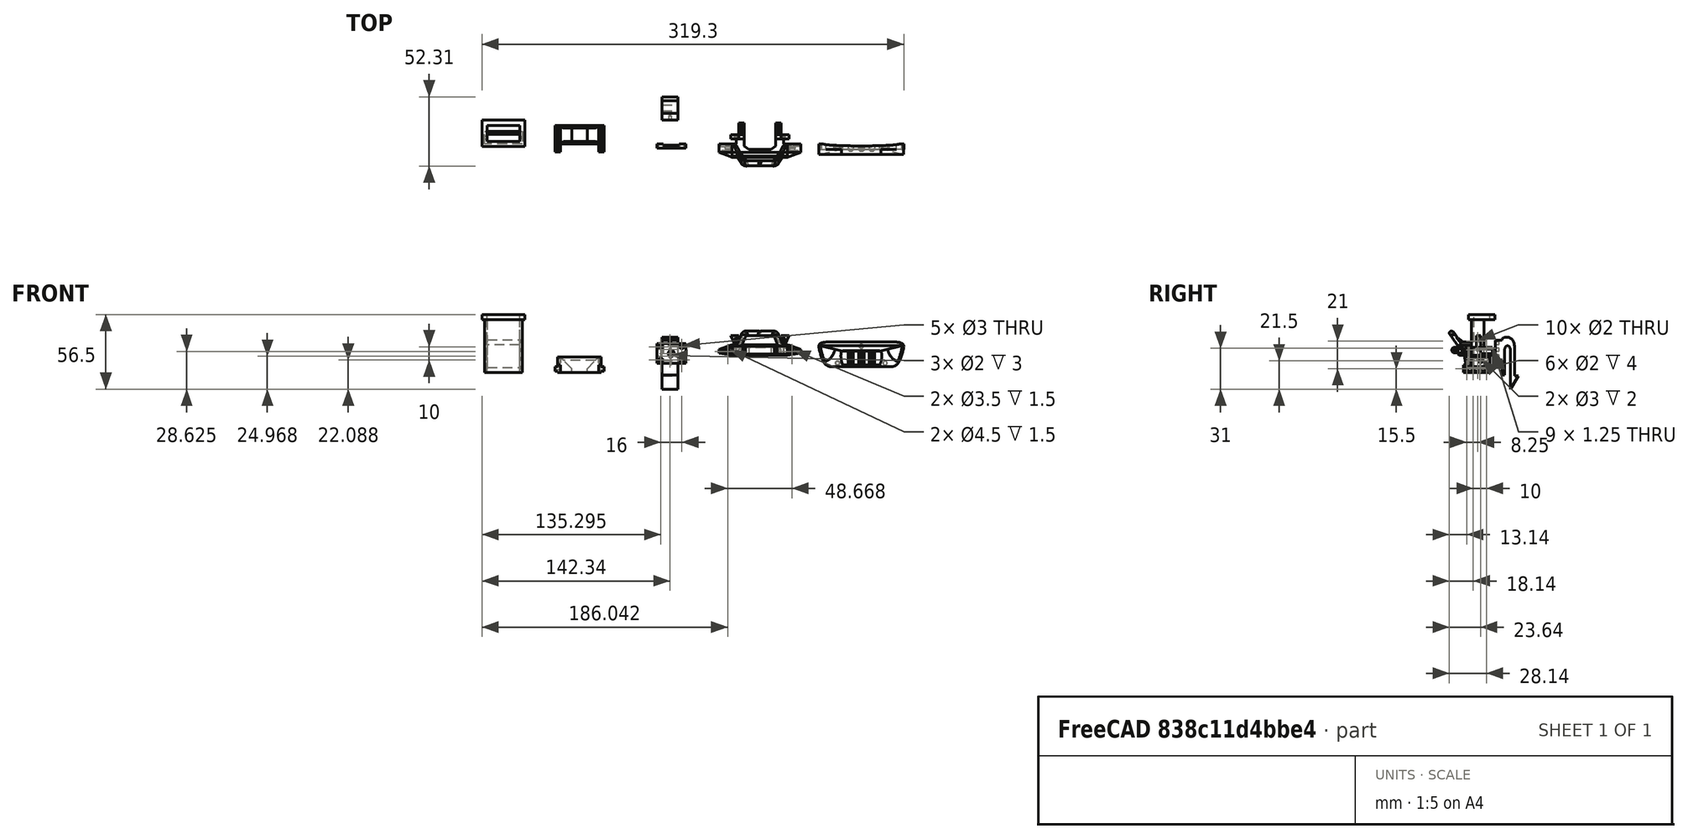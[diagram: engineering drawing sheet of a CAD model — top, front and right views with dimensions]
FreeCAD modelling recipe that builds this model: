
FCSTD DOCUMENT  (FreeCAD 0.21R33515 (Git))
Label: body-clips
License: All rights reserved
LicenseURL: https://en.wikipedia.org/wiki/All_rights_reserved
objects: Sketcher::SketchObject×33, PartDesign::Pocket×18, PartDesign::Pad×16, PartDesign::Body×6, PartDesign::Chamfer×6, PartDesign::Plane×4, PartDesign::Mirrored×4, Part::Part2DObjectPython×4, PartDesign::LinearPattern×2, PartDesign::AdditivePipe×2, Spreadsheet::Sheet×1, PartDesign::MultiTransform×1
note: 138 computed .brp shape members not serialized (recipe doc carries the construction recipe); baked Part::Feature solids carry a one-line shape summary decoded from their .brp

FEATURE [Spreadsheet::Sheet] Spreadsheet  label="param"
  cells = A1=common; A2(wall_thickness)==2 mm; A3(thread_diam)==3 mm; A4(rail_depth)==2 mm; A5(rail_height)==3.5 mm; A6(rail_length)==20 mm; A7(rail_diam)==2 mm; A8(body_width_front)==28 mm; A9(body_width_back)==33 mm; A10=chassis mount; B10=front; C10=back; A11(mount_body_depth)==14 mm; B11==14 mm; C11==14 mm; A12(mount_body_width)==33 mm; B12==28 mm; C12==33 mm; A13(mount_body_height)==12 mm; B13==12 mm; C13==12 mm; A14=tower; A15(tower_body_height)==40 mm; C15==40 mm; A16(tower_clip_depth)==10 mm; C16==10 mm; A17(tower_clip_height)==4 mm; C17==4 mm; A18=computed; A19(tower_body_width)==mount_body_width - 2 * wall_thickness - 0.5 mm; A20(tower_body_depth)==mount_body_depth - 2 * wall_thickness - 0.5 mm; A21(tower_clip_width)==tower_body_width + 2 * wall_thickness; A22=back plate; A23(bplate_width)==22 mm; A24(bplate_height)==15 mm; A25(bplate_thickness)==3 mm; A26(bplate_groove_depth)==1 mm; A27(bplate_groove_width)==12 mm; A28=clip; A29(clip_anker_depth)==5 mm; A30(clip_anker_height)==15 mm; A31(clip_depth)==10 mm; A32(clip_width)==12 mm; A33=grill; A34(grill_mount)==18 mm
FEATURE [Sketcher::SketchObject] Sketch
  FullyConstrained = true
  MapMode = 5
  Support = -> [XY_Plane]
  expr: Constraints[18] = <<param>>.wall_thickness
  expr: Constraints[19] = <<param>>.wall_thickness
  expr: Constraints[20] = <<param>>.wall_thickness
  expr: Constraints[21] = <<param>>.wall_thickness
  expr: Constraints[8] = Spreadsheet.mount_body_width
  expr: Constraints[9] = Spreadsheet.mount_body_depth
  sketch-geometry (8):
    g0: LineSegment StartX=0 StartY=14 StartZ=0 EndX=33 EndY=14 EndZ=0
    g1: LineSegment StartX=33 StartY=14 StartZ=0 EndX=33 EndY=0 EndZ=0
    g2: LineSegment StartX=33 StartY=0 StartZ=0 EndX=0 EndY=0 EndZ=0
    g3: LineSegment StartX=0 StartY=0 StartZ=0 EndX=0 EndY=14 EndZ=0
    g4: LineSegment StartX=2 StartY=12 StartZ=0 EndX=31 EndY=12 EndZ=0
    g5: LineSegment StartX=31 StartY=12 StartZ=0 EndX=31 EndY=2 EndZ=0
    g6: LineSegment StartX=31 StartY=2 StartZ=0 EndX=2 EndY=2 EndZ=0
    g7: LineSegment StartX=2 StartY=2 StartZ=0 EndX=2 EndY=12 EndZ=0
  constraints (23):
    c: Coincident(g0,g1)
    c: Coincident(g1,g2)
    c: Coincident(g2,g3)
    c: Coincident(g3,g0)
    c: Horizontal(g0)
    c: Horizontal(g2)
    c: Vertical(g1)
    c: Vertical(g3)
    c: DistanceX(g0,g0) = 33
    c: DistanceY(g3,g3) = 14
    c: Coincident(g4,g5)
    c: Coincident(g5,g6)
    c: Coincident(g6,g7)
    c: Coincident(g7,g4)
    c: Horizontal(g4)
    c: Horizontal(g6)
    c: Vertical(g5)
    c: Vertical(g7)
    c: DistanceX(g0,g4) = 2
    c: DistanceY(g4,g0) = 2
    c: DistanceX(g5,g1) = 2
    c: DistanceY(g1,g5) = 2
    c: Coincident(g2,g-1)
FEATURE [PartDesign::Pad] Pad  label="mount body"
  Direction = (0,0,1)
  Length = 12
  Length2 = 10
  Profile = -> Sketch
  ReferenceAxis = -> Sketch [N_Axis]
  Type = 0
  expr: Length = Spreadsheet.mount_body_height
FEATURE [Sketcher::SketchObject] Sketch001  label="rails"
  ExternalGeometry = -> [Pad]
  FullyConstrained = false
  MapMode = 5
  Placement = pos=(0,0,0) rot=(0.57735,-0.57735,-0.57735;2.0944rad)
  Support = -> [Pad]
  expr: Constraints[10] = (6 mm - Spreadsheet.rail_height) / 2
  expr: Constraints[8] = Spreadsheet.rail_height
  expr: Constraints[9] = Spreadsheet.rail_length
  sketch-geometry (4):
    g0: LineSegment StartX=-14 StartY=4.75 StartZ=0 EndX=6 EndY=4.75 EndZ=0
    g1: LineSegment StartX=6 StartY=4.75 StartZ=0 EndX=6 EndY=1.25 EndZ=0
    g2: LineSegment StartX=6 StartY=1.25 StartZ=0 EndX=-14 EndY=1.25 EndZ=0
    g3: LineSegment StartX=-14 StartY=1.25 StartZ=0 EndX=-14 EndY=4.75 EndZ=0
  constraints (11):
    c: Coincident(g0,g1)
    c: Coincident(g1,g2)
    c: Coincident(g2,g3)
    c: Coincident(g3,g0)
    c: Horizontal(g0)
    c: Horizontal(g2)
    c: Vertical(g1)
    c: Vertical(g3)
    c: DistanceY(g1,g1) = 3.5
    c: DistanceX(g0,g0) = 20
    c: DistanceY(g-6,g2) = 1.25
FEATURE [Sketcher::SketchObject] Sketch002
  ExternalGeometry = -> [Pad]
  FullyConstrained = true
  MapMode = 5
  Placement = pos=(0,0,0) rot=(0.57735,-0.57735,-0.57735;2.0944rad)
  Support = -> [Pad]
  expr: Constraints[8] = Spreadsheet.rail_length
  sketch-geometry (4):
    g0: LineSegment StartX=-14 StartY=6 StartZ=0 EndX=6 EndY=6 EndZ=0
    g1: LineSegment StartX=6 StartY=6 StartZ=0 EndX=6 EndY=0 EndZ=0
    g2: LineSegment StartX=6 StartY=0 StartZ=0 EndX=-14 EndY=0 EndZ=0
    g3: LineSegment StartX=-14 StartY=0 StartZ=0 EndX=-14 EndY=6 EndZ=0
  constraints (11):
    c: Coincident(g0,g1)
    c: Coincident(g1,g2)
    c: Coincident(g2,g3)
    c: Coincident(g3,g0)
    c: Horizontal(g0)
    c: Horizontal(g2)
    c: Vertical(g1)
    c: Vertical(g3)
    c: DistanceX(g0,g0) = 20
    c: DistanceY(g3,g3) = 6
    c: Coincident(g2,g-3)
FEATURE [PartDesign::Pad] Pad001  label="rail plate"
  BaseFeature = -> Pad
  Direction = (-1,0,0)
  Length = 0
  Length2 = 2
  Profile = -> Sketch002
  ReferenceAxis = -> Sketch002 [N_Axis]
  Type = 4
FEATURE [PartDesign::Pad] Pad002  label="rail"
  BaseFeature = -> Pad001
  Direction = (-1,0,0)
  Length = 2
  Length2 = 10
  Profile = -> Sketch001
  ReferenceAxis = -> Sketch001 [N_Axis]
  Type = 0
  expr: Length = Spreadsheet.rail_depth
FEATURE [Sketcher::SketchObject] Sketch003
  ExternalGeometry = -> [Pad002]
  FullyConstrained = true
  MapMode = 5
  Placement = pos=(0,0,0) rot=(0.57735,-0.57735,-0.57735;2.0944rad)
  Support = -> [Pad002]
  expr: Constraints[0] = <<param>>.thread_diam
  expr: Constraints[2] = Spreadsheet.mount_body_depth / 2
  sketch-geometry (1):
    g0: Circle CenterX=-7 CenterY=9 CenterZ=0 NormalX=0 NormalY=0 NormalZ=1 AngleXU=0 Radius=1.5
  constraints (3):
    c: Diameter(g0) = 3
    c: DistanceY(g0,g-5) = 3
    c: DistanceX(g0,g-5) = 7
FEATURE [PartDesign::Plane] DatumPlane  label="mount center plane"
  AttachmentOffset = pos=(0,0,-16.5) rot=(0,0,1;0rad)
  Length = 60
  MapMode = 5
  Placement = pos=(16.5,0,0) rot=(0.57735,-0.57735,-0.57735;2.0944rad)
  ResizeMode = 0
  Support = -> [Pad]
  Width = 60
  expr: .AttachmentOffset.Base.z = -Spreadsheet.mount_body_width / 2
FEATURE [Sketcher::SketchObject] Sketch004
  FullyConstrained = false
  MapMode = 5
  Placement = pos=(-2,0,0) rot=(0.57735,-0.57735,-0.57735;2.0944rad)
  expr: Constraints[0] = <<param>>.rail_diam
  sketch-geometry (4):
    g0: Circle CenterX=-11.5 CenterY=3 CenterZ=0 NormalX=0 NormalY=0 NormalZ=1 AngleXU=0 Radius=1
    g1: Circle CenterX=-6.5 CenterY=3 CenterZ=0 NormalX=0 NormalY=0 NormalZ=1 AngleXU=0 Radius=1
    g2: Circle CenterX=-1.5 CenterY=3 CenterZ=0 NormalX=0 NormalY=0 NormalZ=1 AngleXU=0 Radius=1
    g3: Circle CenterX=3.5 CenterY=3 CenterZ=0 NormalX=0 NormalY=0 NormalZ=1 AngleXU=0 Radius=1
  constraints (7):
    c: Diameter(g0) = 2
    c: Equal(g0,g1) = 2
    c: DistanceX(g0,g1) = 5
    c: Equal(g0,g2) = 2
    c: Equal(g2,g3) = 2
    c: DistanceX(g2,g3) = 5
    c: DistanceX(g1,g2) = 5
FEATURE [Sketcher::SketchObject] Sketch010
  FullyConstrained = false
  MapMode = 5
  Support = -> [XY_Plane002]
  expr: Constraints[10] = <<param>>.tower_body_depth
  expr: Constraints[19] = <<param>>.wall_thickness
  expr: Constraints[20] = <<param>>.wall_thickness
  expr: Constraints[21] = <<param>>.wall_thickness
  expr: Constraints[22] = <<param>>.wall_thickness
  expr: Constraints[9] = <<param>>.tower_body_width
  sketch-geometry (8):
    g0: LineSegment StartX=-55.3396 StartY=9.5 StartZ=0 EndX=-26.8396 EndY=9.5 EndZ=0
    g1: LineSegment StartX=-26.8396 StartY=9.5 StartZ=0 EndX=-26.8396 EndY=0 EndZ=0
    g2: LineSegment StartX=-26.8396 StartY=0 StartZ=0 EndX=-55.3396 EndY=0 EndZ=0
    g3: LineSegment StartX=-55.3396 StartY=0 StartZ=0 EndX=-55.3396 EndY=9.5 EndZ=0
    g4: LineSegment StartX=-53.3396 StartY=7.5 StartZ=0 EndX=-28.8396 EndY=7.5 EndZ=0
    g5: LineSegment StartX=-28.8396 StartY=7.5 StartZ=0 EndX=-28.8396 EndY=2 EndZ=0
    g6: LineSegment StartX=-28.8396 StartY=2 StartZ=0 EndX=-53.3396 EndY=2 EndZ=0
    g7: LineSegment StartX=-53.3396 StartY=2 StartZ=0 EndX=-53.3396 EndY=7.5 EndZ=0
  constraints (23):
    c: Coincident(g0,g1)
    c: Coincident(g1,g2)
    c: Coincident(g2,g3)
    c: Coincident(g3,g0)
    c: Horizontal(g0)
    c: Horizontal(g2)
    c: Vertical(g1)
    c: Vertical(g3)
    c: PointOnObject(g1,g-1)
    c: DistanceX(g0,g0) = 28.5
    c: DistanceY(g3,g3) = 9.5
    c: Coincident(g4,g5)
    c: Coincident(g5,g6)
    c: Coincident(g6,g7)
    c: Coincident(g7,g4)
    c: Horizontal(g4)
    c: Horizontal(g6)
    c: Vertical(g5)
    c: Vertical(g7)
    c: DistanceX(g0,g4) = 2
    c: DistanceX(g4,g0) = 2
    c: DistanceY(g4,g0) = 2
    c: DistanceY(g1,g5) = 2
FEATURE [PartDesign::Pad] Pad006  label="tower body"
  Direction = (0,0,1)
  Length = 40
  Length2 = 10
  Profile = -> Sketch010
  ReferenceAxis = -> Sketch010 [N_Axis]
  Refine = true
  Type = 0
  expr: Length = <<param>>.tower_body_height
FEATURE [PartDesign::Plane] DatumPlane002  label="tower center plane"
  AttachmentOffset = pos=(0,0,-14.25) rot=(0,0,1;0rad)
  Length = 61.7473
  MapMode = 5
  Placement = pos=(-41.0896,0,0) rot=(0.57735,-0.57735,-0.57735;2.0944rad)
  ResizeMode = 0
  Support = -> [Pad006]
  Width = 80.7473
  expr: .AttachmentOffset.Base.z = -<<param>>.tower_body_width / 2
FEATURE [Sketcher::SketchObject] Sketch011
  ExternalGeometry = -> [Pad006]
  FullyConstrained = true
  MapMode = 5
  Placement = pos=(0,0,40) rot=(0,0,1;0rad)
  Support = -> [Pad006]
  expr: Constraints[16] = <<param>>.wall_thickness * 2
  expr: Constraints[17] = <<param>>.wall_thickness * 2
  expr: Constraints[18] = <<param>>.wall_thickness * 2
  expr: Constraints[19] = <<param>>.wall_thickness * 2
  expr: Constraints[20] = <<param>>.tower_clip_depth + 5 * <<param>>.wall_thickness
  expr: Constraints[21] = <<param>>.tower_clip_width
  sketch-geometry (8):
    g0: LineSegment StartX=-57.3396 StartY=18 StartZ=0 EndX=-24.8396 EndY=18 EndZ=0
    g1: LineSegment StartX=-24.8396 StartY=18 StartZ=0 EndX=-24.8396 EndY=-2 EndZ=0
    g2: LineSegment StartX=-24.8396 StartY=-2 StartZ=0 EndX=-57.3396 EndY=-2 EndZ=0
    g3: LineSegment StartX=-57.3396 StartY=-2 StartZ=0 EndX=-57.3396 EndY=18 EndZ=0
    g4: LineSegment StartX=-53.3396 StartY=14 StartZ=0 EndX=-28.8396 EndY=14 EndZ=0
    g5: LineSegment StartX=-28.8396 StartY=14 StartZ=0 EndX=-28.8396 EndY=2 EndZ=0
    g6: LineSegment StartX=-28.8396 StartY=2 StartZ=0 EndX=-53.3396 EndY=2 EndZ=0
    g7: LineSegment StartX=-53.3396 StartY=2 StartZ=0 EndX=-53.3396 EndY=14 EndZ=0
  constraints (23):
    c: Coincident(g0,g1)
    c: Coincident(g1,g2)
    c: Coincident(g2,g3)
    c: Coincident(g3,g0)
    c: Horizontal(g0)
    c: Horizontal(g2)
    c: Vertical(g1)
    c: Vertical(g3)
    c: Coincident(g4,g5)
    c: Coincident(g5,g6)
    c: Coincident(g6,g7)
    c: Coincident(g7,g4)
    c: Horizontal(g4)
    c: Horizontal(g6)
    c: Vertical(g5)
    c: Vertical(g7)
    c: DistanceX(g0,g4) = 4
    c: DistanceX(g4,g0) = 4
    c: DistanceY(g4,g0) = 4
    c: DistanceY(g1,g5) = 4
    c: DistanceY(g1,g1) = 20
    c: DistanceX(g0,g0) = 32.5
    c: Coincident(g5,g-5)
FEATURE [PartDesign::Pad] Pad007  label="tower clip"
  BaseFeature = -> Pad006
  Direction = (0,0,1)
  Length = 4
  Length2 = 10
  Profile = -> Sketch011
  ReferenceAxis = -> Sketch011 [N_Axis]
  Refine = true
  Type = 0
  expr: Length = <<param>>.tower_clip_height
FEATURE [Sketcher::SketchObject] Sketch012
  ExternalGeometry = -> [Pad006]
  FullyConstrained = true
  MapMode = 5
  Placement = pos=(0,9.5,0) rot=(0,0.707107,0.707107;3.14159rad)
  Support = -> [Pad007]
  expr: Constraints[10] = <<param>>.wall_thickness
  expr: Constraints[20] = <<param>>.tower_body_height - 15 mm - 8 mm
  expr: Constraints[21] = <<param>>.tower_body_width - 2 * <<param>>.wall_thickness
  expr: Constraints[8] = <<param>>.tower_body_width - 2 * <<param>>.wall_thickness
  sketch-geometry (8):
    g0: LineSegment StartX=28.8396 StartY=40 StartZ=0 EndX=53.3396 EndY=40 EndZ=0
    g1: LineSegment StartX=53.3396 StartY=40 StartZ=0 EndX=53.3396 EndY=25 EndZ=0
    g2: LineSegment StartX=53.3396 StartY=25 StartZ=0 EndX=28.8396 EndY=25 EndZ=0
    g3: LineSegment StartX=28.8396 StartY=25 StartZ=0 EndX=28.8396 EndY=40 EndZ=0
    g4: LineSegment StartX=28.8396 StartY=21 StartZ=0 EndX=53.3396 EndY=21 EndZ=0
    g5: LineSegment StartX=53.3396 StartY=21 StartZ=0 EndX=53.3396 EndY=4 EndZ=0
    g6: LineSegment StartX=53.3396 StartY=4 StartZ=0 EndX=28.8396 EndY=4 EndZ=0
    g7: LineSegment StartX=28.8396 StartY=4 StartZ=0 EndX=28.8396 EndY=21 EndZ=0
  constraints (24):
    c: Coincident(g0,g1)
    c: Coincident(g1,g2)
    c: Coincident(g2,g3)
    c: Coincident(g3,g0)
    c: Horizontal(g0)
    c: Horizontal(g2)
    c: Vertical(g1)
    c: Vertical(g3)
    c: DistanceX(g0,g0) = 24.5
    c: DistanceY(g3,g3) = 15
    c: DistanceX(g-3,g0) = 2
    c: DistanceY(g0,g-3) = 0
    c: Coincident(g4,g5)
    c: Coincident(g5,g6)
    c: Coincident(g6,g7)
    c: Coincident(g7,g4)
    c: Horizontal(g4)
    c: Horizontal(g6)
    c: Vertical(g5)
    c: Vertical(g7)
    c: DistanceY(g7,g7) = 17
    c: DistanceX(g4,g4) = 24.5
    c: DistanceY(g4,g2) = 4
    c: DistanceX(g4,g2) = 0
FEATURE [PartDesign::Pocket] Pocket004  label="tower clip cutout"
  BaseFeature = -> Pad007
  Direction = (0,-1,2e-16)
  Length = 5
  Length2 = 5
  Profile = -> Sketch012
  ReferenceAxis = -> Sketch012 [N_Axis]
  Refine = true
  Type = 0
FEATURE [Sketcher::SketchObject] Sketch013
  FullyConstrained = true
  MapMode = 5
  Placement = pos=(-55.3396,0,0) rot=(0.57735,-0.57735,-0.57735;2.0944rad)
  Support = -> [Pocket004]
  expr: Constraints[0] = <<param>>.rail_diam
  expr: Constraints[1] = <<param>>.tower_body_depth / 2
  sketch-geometry (1):
    g0: Circle CenterX=-4.75 CenterY=4 CenterZ=0 NormalX=0 NormalY=0 NormalZ=1 AngleXU=0 Radius=1
  constraints (3):
    c: Diameter(g0) = 2
    c: DistanceX(g0,g-1) = 4.75
    c: DistanceY(g-1,g0) = 4
FEATURE [PartDesign::Pocket] Pocket005  label="tower drills"
  BaseFeature = -> Pocket004
  Direction = (1,0,0)
  Length = 5
  Length2 = 5
  Profile = -> Sketch013
  ReferenceAxis = -> Sketch013 [N_Axis]
  Refine = true
  Type = 0
FEATURE [PartDesign::LinearPattern] LinearPattern
  Direction = -> Z_Axis002
  Length = 20
  Occurrences = 4
  Refine = true
  expr: Length = <<param>>.tower_body_height - 20 mm
FEATURE [PartDesign::Mirrored] Mirrored002
  MirrorPlane = -> DatumPlane002
  Refine = true
FEATURE [PartDesign::MultiTransform] MultiTransform
  BaseFeature = -> Pocket005
  Originals = -> [Pocket005]
  Refine = true
  Transformations = -> [LinearPattern,Mirrored002]
FEATURE [PartDesign::Body] Body002  label="tower"
  Group = -> [Sketch010,Pad006,DatumPlane002,Sketch011,Pad007,Sketch012,Pocket004,Sketch013,Pocket005,MultiTransform,LinearPattern,Mirrored002]
  Origin = -> Origin002
  Tip = -> MultiTransform
FEATURE [Sketcher::SketchObject] Sketch014
  FullyConstrained = false
  MapMode = 5
  Placement = pos=(0,0,0) rot=(1,0,0;1.5708rad)
  Support = -> [XZ_Plane003]
  expr: Constraints[13] = (<<param>>.bplate_width - 16 mm) / 2
  expr: Constraints[14] = (<<param>>.bplate_height - 10 mm) / 2
  expr: Constraints[15] = (<<param>>.bplate_height - 10 mm) / 2
  expr: Constraints[19] = (<<param>>.bplate_width - 16 mm) / 2
  expr: Constraints[22] = <<param>>.thread_diam
  expr: Constraints[23] = <<param>>.bplate_width / 2
  expr: Constraints[24] = <<param>>.bplate_height / 2
  expr: Constraints[8] = <<param>>.bplate_width
  expr: Constraints[9] = <<param>>.bplate_height
  sketch-geometry (9):
    g0: LineSegment StartX=10.9554 StartY=22.0881 StartZ=0 EndX=32.9554 EndY=22.0881 EndZ=0
    g1: LineSegment StartX=32.9554 StartY=22.0881 StartZ=0 EndX=32.9554 EndY=7.08806 EndZ=0
    g2: LineSegment StartX=32.9554 StartY=7.08806 StartZ=0 EndX=10.9554 EndY=7.08806 EndZ=0
    g3: LineSegment StartX=10.9554 StartY=7.08806 StartZ=0 EndX=10.9554 EndY=22.0881 EndZ=0
    g4: Circle CenterX=13.9554 CenterY=19.5881 CenterZ=0 NormalX=0 NormalY=0 NormalZ=1 AngleXU=0 Radius=1.5
    g5: Circle CenterX=29.9554 CenterY=19.5881 CenterZ=0 NormalX=0 NormalY=0 NormalZ=1 AngleXU=0 Radius=1.5
    g6: Circle CenterX=13.9554 CenterY=9.58806 CenterZ=0 NormalX=0 NormalY=0 NormalZ=1 AngleXU=0 Radius=1.5
    g7: Circle CenterX=29.9554 CenterY=9.58806 CenterZ=0 NormalX=0 NormalY=0 NormalZ=1 AngleXU=0 Radius=1.5
    g8: Circle CenterX=21.9554 CenterY=14.5881 CenterZ=0 NormalX=0 NormalY=0 NormalZ=1 AngleXU=0 Radius=1.5
  constraints (25):
    c: Coincident(g0,g1)
    c: Coincident(g1,g2)
    c: Coincident(g2,g3)
    c: Coincident(g3,g0)
    c: Horizontal(g0)
    c: Horizontal(g2)
    c: Vertical(g1)
    c: Vertical(g3)
    c: DistanceX(g0,g0) = 22
    c: DistanceY(g1,g1) = 15
    c: Diameter(g4) = 3
    c: Equal(g4,g5) = 3
    c: DistanceX(g4,g5) = 16
    c: DistanceX(g0,g4) = 3
    c: DistanceY(g4,g0) = 2.5
    c: DistanceY(g5,g0) = 2.5
    c: Equal(g4,g6) = 3
    c: Equal(g6,g7) = 3
    c: DistanceX(g6,g7) = 16
    c: DistanceX(g2,g6) = 3
    c: DistanceY(g6,g4) = 10
    c: DistanceY(g7,g5) = 10
    c: Diameter(g8) = 3
    c: DistanceX(g0,g8) = 11
    c: DistanceY(g8,g0) = 7.5
FEATURE [PartDesign::Pad] Pad008
  Direction = (0,-1,-2e-16)
  Length = 3
  Length2 = 10
  Placement = pos=(0,0,0) rot=(1,0,0;1.5708rad)
  Profile = -> Sketch014
  ReferenceAxis = -> Sketch014 [N_Axis]
  Refine = true
  Type = 0
  expr: Length = <<param>>.bplate_thickness
FEATURE [Sketcher::SketchObject] Sketch015
  ExternalGeometry = -> [Pad008]
  FullyConstrained = false
  MapMode = 5
  Placement = pos=(0,0,0) rot=(-1,0,0;1.5708rad)
  Support = -> [Pad008]
  expr: Constraints[8] = <<param>>.bplate_height
  expr: Constraints[9] = <<param>>.bplate_groove_width
  sketch-geometry (4):
    g0: LineSegment StartX=15.9554 StartY=-7.08806 StartZ=0 EndX=27.9554 EndY=-7.08806 EndZ=0
    g1: LineSegment StartX=27.9554 StartY=-7.08806 StartZ=0 EndX=27.9554 EndY=-22.0881 EndZ=0
    g2: LineSegment StartX=27.9554 StartY=-22.0881 StartZ=0 EndX=15.9554 EndY=-22.0881 EndZ=0
    g3: LineSegment StartX=15.9554 StartY=-22.0881 StartZ=0 EndX=15.9554 EndY=-7.08806 EndZ=0
  constraints (11):
    c: Coincident(g0,g1)
    c: Coincident(g1,g2)
    c: Coincident(g2,g3)
    c: Coincident(g3,g0)
    c: Horizontal(g0)
    c: Horizontal(g2)
    c: Vertical(g1)
    c: Vertical(g3)
    c: DistanceY(g3,g3) = 15
    c: DistanceX(g0,g0) = 12
    c: DistanceY(g0,g-3) = 0
FEATURE [PartDesign::Pocket] Pocket006
  BaseFeature = -> Pad008
  Direction = (0,-1,-2e-16)
  Length = 1
  Length2 = 5
  Placement = pos=(0,0,0) rot=(1,0,0;1.5708rad)
  Profile = -> Sketch015
  ReferenceAxis = -> Sketch015 [N_Axis]
  Refine = true
  Type = 0
  expr: Length = <<param>>.bplate_groove_depth
FEATURE [Sketcher::SketchObject] Sketch016
  FullyConstrained = false
  MapMode = 5
  Placement = pos=(0,0,0) rot=(0.57735,0.57735,0.57735;2.0944rad)
  Support = -> [YZ_Plane004]
  expr: Constraints[12] = <<param>>.clip_anker_depth
  expr: Constraints[13] = <<param>>.clip_anker_height
  expr: Constraints[47] = <<param>>.mount_body_height
  expr: Constraints[48] = <<param>>.tower_body_depth
  expr: Constraints[56] = <<param>>.wall_thickness
  sketch-geometry (26):
    g0: LineSegment StartX=18.1651 StartY=24.4988 StartZ=0 EndX=23.1651 EndY=24.4988 EndZ=0
    g1: LineSegment StartX=23.1651 StartY=9.49883 StartZ=0 EndX=18.1651 EndY=9.49883 EndZ=0
    g2: LineSegment StartX=18.1651 StartY=9.49883 StartZ=0 EndX=18.1651 EndY=24.4988 EndZ=0
    g3: LineSegment StartX=32.6651 StartY=20.0525 StartZ=0 EndX=32.6651 EndY=-2.50117 EndZ=0
    g4: LineSegment StartX=32.6651 StartY=-2.50117 StartZ=0 EndX=35.6651 EndY=-2.50117 EndZ=0
    g5: LineSegment StartX=35.6651 StartY=-2.50117 StartZ=0 EndX=29.6651 EndY=-12.5012 EndZ=0
    g6: LineSegment StartX=29.6651 StartY=-12.5012 StartZ=0 EndX=29.6651 EndY=16.896 EndZ=0
    g7: GeomPoint X=23.1651 Y=24.4988 Z=0
    g8: GeomPoint X=26.4127 Y=26.9246 Z=0
    g9: GeomPoint X=32.6651 Y=20.0525 Z=0
    g10: BSplineCurve PolesCount=4 KnotsCount=2 Degree=3 IsPeriodic=0
    g11-g14: Circle x4 (B-spline internal-alignment scaffolding for g10; pole/knot coordinates omitted)
    g15: GeomPoint X=25.1651 Y=16.5755 Z=0
    g16: GeomPoint X=27.311 Y=20.3862 Z=0
    g17: GeomPoint X=29.6651 Y=16.896 Z=0
    g18: BSplineCurve PolesCount=4 KnotsCount=2 Degree=3 IsPeriodic=0
    g19-g22: Circle x4 (B-spline internal-alignment scaffolding for g18; pole/knot coordinates omitted)
    g23: LineSegment StartX=23.1651 StartY=9.49883 StartZ=0 EndX=23.1651 EndY=-1.80872 EndZ=0
    g24: LineSegment StartX=23.1651 StartY=-1.80872 StartZ=0 EndX=25.1651 EndY=-1.80872 EndZ=0
    g25: LineSegment StartX=25.1651 StartY=-1.80872 StartZ=0 EndX=25.1651 EndY=16.5755 EndZ=0
  constraints (58):
    c: Coincident(g1,g2)
    c: Coincident(g2,g0)
    c: Horizontal(g0)
    c: Horizontal(g1)
    c: Vertical(g2)
    c: Vertical(g3)
    c: Coincident(g4,g3)
    c: Horizontal(g4)
    c: Coincident(g5,g4)
    c: Coincident(g6,g5)
    c: Vertical(g6)
    c: DistanceX(g4,g4) = 3
    c: DistanceX(g0,g0) = 5
    c: DistanceY(g2,g2) = 15
    c: DistanceX(g6,g3) = 3
    c: Coincident(g10,g0)
    c: Coincident(g10,g3)
    c: InternalAlignment(g7,g10)
    c: PointOnObject(g8,g10)
    c: InternalAlignment(g9,g10)
    c: InternalAlignment(g11,g10)
    c: Weight(g11) = 1
    c: InternalAlignment(g12,g10)
    c: Equal(g12,g11)
    c: InternalAlignment(g13,g10)
    c: Equal(g13,g11)
    c: InternalAlignment(g14,g10)
    c: Equal(g14,g11)
    c: DistanceY(g12,g13) = 0
    c: DistanceX(g12,g0) = 0
    c: DistanceX(g3,g13) = 0
    c: Coincident(g18,g6)
    c: InternalAlignment(g15,g18)
    c: PointOnObject(g16,g18)
    c: InternalAlignment(g17,g18)
    c: InternalAlignment(g19,g18)
    c: Weight(g19) = 1
    c: InternalAlignment(g20,g18)
    c: Equal(g20,g19)
    c: InternalAlignment(g21,g18)
    c: Equal(g21,g19)
    c: InternalAlignment(g22,g18)
    c: Equal(g22,g19)
    c: DistanceY(g21,g20) = 0
    c: DistanceX(g18,g20) = 0
    c: DistanceX(g21,g6) = 0
    c: DistanceY(g5,g3) = 10
    c: DistanceY(g3,g1) = 12
    c: DistanceX(g1,g9) = 9.5
    c: Coincident(g23,g1)
    c: Vertical(g23)
    c: Coincident(g24,g23)
    c: Horizontal(g24)
    c: Coincident(g25,g18)
    c: Vertical(g25)
    c: Coincident(g25,g24)
    c: DistanceX(g24,g24) = 2
    c: DistanceX(g0,g1) = 0
FEATURE [PartDesign::Pad] Pad009
  Direction = (1,-2e-16,3e-16)
  Length = 12
  Length2 = 10
  Placement = pos=(0,0,0) rot=(0.57735,0.57735,0.57735;2.0944rad)
  Profile = -> Sketch016
  ReferenceAxis = -> Sketch016 [N_Axis]
  Refine = true
  Type = 0
  expr: Length = <<param>>.clip_width
FEATURE [PartDesign::Chamfer] Chamfer
  Angle = 45
  Base = -> Pocket006 [Face13]
  BaseFeature = -> Pocket006
  ChamferType = 2
  FlipDirection = false
  Placement = pos=(0,0,0) rot=(1,0,0;1.5708rad)
  Refine = true
  Size = 0.8
  Size2 = 1
  SupportTransform = false
  UseAllEdges = false
FEATURE [PartDesign::Body] Body003  label="back plate"
  Group = -> [Sketch014,Pad008,Sketch015,Pocket006,Chamfer]
  Origin = -> Origin003
  Placement = pos=(64,0,0) rot=(0,0,1;0rad)
  Tip = -> Chamfer
FEATURE [Sketcher::SketchObject] Sketch017
  ExternalGeometry = -> [Pad009]
  FullyConstrained = false
  MapMode = 5
  Placement = pos=(8e-15,18.1651,-4e-15) rot=(-0.57735,-0.57735,0.57735;4.18879rad)
  Support = -> [Pad009]
  expr: Constraints[0] = <<param>>.rail_diam
  expr: Constraints[1] = <<param>>.clip_width / 2
  sketch-geometry (1):
    g0: Circle CenterX=-22.4675 CenterY=6 CenterZ=0 NormalX=0 NormalY=0 NormalZ=1 AngleXU=0 Radius=1
  constraints (2):
    c: Diameter(g0) = 2
    c: DistanceY(g0,g-3) = 6
FEATURE [PartDesign::Pocket] Pocket007
  BaseFeature = -> Pad009
  Direction = (4e-16,1,-2e-16)
  Length = 3
  Length2 = 5
  Placement = pos=(0,0,0) rot=(0.57735,0.57735,0.57735;2.0944rad)
  Profile = -> Sketch017
  ReferenceAxis = -> Sketch017 [N_Axis]
  Refine = true
  Type = 0
FEATURE [PartDesign::LinearPattern] LinearPattern001
  BaseFeature = -> Pocket007
  Direction = -> Z_Axis004
  Length = 15
  Occurrences = 4
  Originals = -> [Pocket007]
  Placement = pos=(0,0,0) rot=(0.57735,0.57735,0.57735;2.0944rad)
  Refine = true
  Reversed = true
  expr: Length = <<param>>.clip_anker_height
FEATURE [PartDesign::Body] Body004  label="clip"
  Group = -> [Sketch016,Pad009,Sketch017,Pocket007,LinearPattern001]
  Origin = -> Origin004
  Placement = pos=(79,0,0) rot=(0,0,1;0rad)
  Tip = -> LinearPattern001
FEATURE [Sketcher::SketchObject] Sketch018
  FullyConstrained = false
  MapMode = 5
  Placement = pos=(0,0,0) rot=(1,0,0;1.5708rad)
  Support = -> [XZ_Plane005]
  sketch-geometry (17):
    g0: LineSegment StartX=229.786 StartY=23.4729 StartZ=0 EndX=250.786 EndY=23.4729 EndZ=0
    g1: LineSegment StartX=229.786 StartY=4.47292 StartZ=0 EndX=250.786 EndY=4.47292 EndZ=0
    g2: LineSegment StartX=229.786 StartY=4.47292 StartZ=0 EndX=229.786 EndY=23.4729 EndZ=0
    g3: LineSegment StartX=250.786 StartY=23.4729 StartZ=0 EndX=260.786 EndY=23.4729 EndZ=0
    g4: LineSegment StartX=260.786 StartY=23.4729 StartZ=0 EndX=260.786 EndY=4.47292 EndZ=0
    g5: LineSegment StartX=250.786 StartY=4.47292 StartZ=0 EndX=260.786 EndY=4.47292 EndZ=0
    g6-g9: GeomPoint x4 (B-spline internal-alignment scaffolding for g10; pole/knot coordinates omitted)
    g10: BSplineCurve PolesCount=6 KnotsCount=4 Degree=3 IsPeriodic=0
    g11-g16: Circle x6 (B-spline internal-alignment scaffolding for g10; pole/knot coordinates omitted)
  constraints (31):
    c: Horizontal(g0)
    c: Horizontal(g1)
    c: DistanceY(g1,g0) = 19
    c: Coincident(g2,g1)
    c: Coincident(g2,g0)
    c: Vertical(g2)
    c: DistanceX(g0,g0) = 21
    c: DistanceX(g1,g1) = 21
    c: Coincident(g3,g0)
    c: Horizontal(g3)
    c: Coincident(g4,g3)
    c: Vertical(g4)
    c: Coincident(g5,g1)
    c: Coincident(g5,g4)
    c: Horizontal(g5)
    c: DistanceX(g5,g5) = 10
    c: Coincident(g10,g0)
    c: Coincident(g10,g1)
    c: InternalAlignment(g6-g9 -> g10) x4
    c: InternalAlignment(g11,g10)
    c: Weight(g11) = 1
    c: InternalAlignment(g12,g10)
    c: Equal(g12,g11)
    c: InternalAlignment(g13,g10)
    c: Equal(g13,g11)
    c: InternalAlignment(g14,g10)
    c: Equal(g14,g11)
    c: InternalAlignment(g15,g10)
    c: Equal(g15,g11)
    c: InternalAlignment(g16,g10)
    c: Equal(g16,g11)
FEATURE [PartDesign::Pad] Pad010  label="grill base"
  Direction = (0,-1,-2e-16)
  Length = 4
  Length2 = 10
  Placement = pos=(0,0,0) rot=(1,0,0;1.5708rad)
  Profile = -> Sketch018
  ReferenceAxis = -> Sketch018 [N_Axis]
  Refine = true
  Type = 0
FEATURE [Sketcher::SketchObject] Sketch019
  ExternalGeometry = -> [Pad010]
  FullyConstrained = false
  MapMode = 5
  Placement = pos=(0,-4,-9e-16) rot=(1,0,0;1.5708rad)
  Support = -> [Pad010]
  sketch-geometry (10):
    g0: LineSegment StartX=229.786 StartY=21.9959 StartZ=0 EndX=243.834 EndY=21.9959 EndZ=0
    g1: LineSegment StartX=243.834 StartY=5.89636 StartZ=0 EndX=229.786 EndY=5.89636 EndZ=0
    g2: LineSegment StartX=229.786 StartY=5.89636 StartZ=0 EndX=229.786 EndY=21.9959 EndZ=0
    g3: GeomPoint X=243.834 Y=21.9959 Z=0
    g4: GeomPoint X=243.834 Y=5.89636 Z=0
    g5: BSplineCurve PolesCount=4 KnotsCount=2 Degree=3 IsPeriodic=0
    g6-g9: Circle x4 (B-spline internal-alignment scaffolding for g5; pole/knot coordinates omitted)
  constraints (18):
    c: Coincident(g1,g2)
    c: Coincident(g2,g0)
    c: Horizontal(g0)
    c: Horizontal(g1)
    c: Vertical(g2)
    c: Coincident(g5,g0)
    c: Coincident(g5,g1)
    c: InternalAlignment(g3,g5)
    c: InternalAlignment(g4,g5)
    c: InternalAlignment(g6,g5)
    c: Weight(g6) = 1
    c: InternalAlignment(g7,g5)
    c: Equal(g7,g6)
    c: InternalAlignment(g8,g5)
    c: Equal(g8,g6)
    c: InternalAlignment(g9,g5)
    c: Equal(g9,g6)
    c: DistanceX(g0,g-3) = 0
FEATURE [Sketcher::SketchObject] Sketch020
  FullyConstrained = false
  MapMode = 5
  Placement = pos=(0,-4,-9e-16) rot=(1,0,0;1.5708rad)
  Support = -> [Pad010]
  sketch-geometry (18):
    g0-g3: GeomPoint x4 (B-spline internal-alignment scaffolding for g4; pole/knot coordinates omitted)
    g4: BSplineCurve PolesCount=6 KnotsCount=4 Degree=3 IsPeriodic=0
    g5-g10: Circle x6 (B-spline internal-alignment scaffolding for g4; pole/knot coordinates omitted)
    g11: GeomPoint X=248.794 Y=21.8316 Z=0
    g12: GeomPoint X=256.494 Y=8.78724 Z=0
    g13: BSplineCurve PolesCount=4 KnotsCount=2 Degree=3 IsPeriodic=0
    g14-g17: Circle x4 (B-spline internal-alignment scaffolding for g13; pole/knot coordinates omitted)
  constraints (25):
    c: InternalAlignment(g0-g3 -> g4) x4
    c: InternalAlignment(g5,g4)
    c: Weight(g5) = 1
    c: InternalAlignment(g6,g4)
    c: Equal(g6,g5)
    c: InternalAlignment(g7,g4)
    c: Equal(g7,g5)
    c: InternalAlignment(g8,g4)
    c: Equal(g8,g5)
    c: InternalAlignment(g9,g4)
    c: Equal(g9,g5)
    c: InternalAlignment(g10,g4)
    c: Equal(g10,g5)
    c: Coincident(g13,g4)
    c: Coincident(g13,g4)
    c: InternalAlignment(g11,g13)
    c: InternalAlignment(g12,g13)
    c: InternalAlignment(g14,g13)
    c: Weight(g14) = 1
    c: InternalAlignment(g15,g13)
    c: Equal(g15,g14)
    c: InternalAlignment(g16,g13)
    c: Equal(g16,g14)
    c: InternalAlignment(g17,g13)
    c: Equal(g17,g14)
FEATURE [Sketcher::SketchObject] Sketch021
  ExternalGeometry = -> [Sketch018]
  FullyConstrained = false
  MapMode = 5
  Placement = pos=(0,0,0) rot=(1,0,0;1.5708rad)
  Support = -> [XZ_Plane005]
  sketch-geometry (11):
    g0: LineSegment StartX=244.845 StartY=16.4533 StartZ=0 EndX=261.898 EndY=20.6924 EndZ=0
    g1: GeomPoint X=244.616 Y=23.4729 Z=0
    g2: GeomPoint X=261.898 Y=20.6924 Z=0
    g3: BSplineCurve PolesCount=4 KnotsCount=2 Degree=3 IsPeriodic=0
    g4-g7: Circle x4 (B-spline internal-alignment scaffolding for g3; pole/knot coordinates omitted)
    g8: LineSegment StartX=244.845 StartY=16.4533 StartZ=0 EndX=229.786 EndY=16.4533 EndZ=0
    g9: LineSegment StartX=229.786 StartY=16.4533 StartZ=0 EndX=229.786 EndY=23.4729 EndZ=0
    g10: LineSegment StartX=229.786 StartY=23.4729 StartZ=0 EndX=244.616 EndY=23.4729 EndZ=0
  constraints (19):
    c: Coincident(g3,g0)
    c: InternalAlignment(g1,g3)
    c: InternalAlignment(g2,g3)
    c: InternalAlignment(g4,g3)
    c: Weight(g4) = 1
    c: InternalAlignment(g5,g3)
    c: Equal(g5,g4)
    c: InternalAlignment(g6,g3)
    c: Equal(g6,g4)
    c: InternalAlignment(g7,g3)
    c: Equal(g7,g4)
    c: Horizontal(g8)
    c: Vertical(g9)
    c: Horizontal(g10)
    c: Coincident(g9,g10)
    c: Coincident(g9,g-3)
    c: Coincident(g8,g9)
    c: Coincident(g3,g10)
    c: Coincident(g0,g8)
FEATURE [PartDesign::Pocket] Pocket008  label="grill center"
  BaseFeature = -> Pad010
  Direction = (0,1,2e-16)
  Length = 4
  Length2 = 5
  Placement = pos=(0,0,0) rot=(1,0,0;1.5708rad)
  Profile = -> Sketch019
  ReferenceAxis = -> Sketch019 [N_Axis]
  Refine = true
  Type = 0
FEATURE [PartDesign::Pocket] Pocket009  label="grill lamp"
  BaseFeature = -> Pocket008
  Direction = (0,1,2e-16)
  Length = 4
  Length2 = 5
  Placement = pos=(0,0,0) rot=(1,0,0;1.5708rad)
  Profile = -> Sketch020
  ReferenceAxis = -> Sketch020 [N_Axis]
  Refine = true
  Type = 0
FEATURE [PartDesign::Pad] Pad011  label="grill lid"
  BaseFeature = -> Pocket009
  Direction = (0,-1,-2e-16)
  Length = 8
  Length2 = 10
  Placement = pos=(0,0,0) rot=(1,0,0;1.5708rad)
  Profile = -> Sketch021
  ReferenceAxis = -> Sketch021 [N_Axis]
  Refine = true
  Type = 0
FEATURE [PartDesign::Chamfer] Chamfer001
  Angle = 46
  Base = -> Pad011 [Edge39]
  BaseFeature = -> Pad011
  ChamferType = 2
  FlipDirection = false
  Placement = pos=(0,0,0) rot=(1,0,0;1.5708rad)
  Refine = true
  Size = 4
  Size2 = 1
  SupportTransform = false
  UseAllEdges = false
FEATURE [Sketcher::SketchObject] Sketch024
  ExternalGeometry = -> [Sketch018]
  FullyConstrained = true
  MapMode = 5
  Placement = pos=(0,0,0) rot=(-1,0,0;1.5708rad)
  Support = -> [Pad010]
  expr: Constraints[0] = <<param>>.thread_diam
  expr: Constraints[2] = <<param>>.grill_mount
  sketch-geometry (3):
    g0: Circle CenterX=211.786 CenterY=-7.32292 CenterZ=0 NormalX=0 NormalY=0 NormalZ=1 AngleXU=0 Radius=1.5
    g1: Circle CenterX=247.786 CenterY=-7.32292 CenterZ=0 NormalX=0 NormalY=0 NormalZ=1 AngleXU=0 Radius=1.5
    g2: Circle CenterX=229.786 CenterY=-19.9229 CenterZ=0 NormalX=0 NormalY=0 NormalZ=1 AngleXU=0 Radius=1.5
  constraints (9):
    c: Diameter(g0) = 3
    c: Equal(g0,g1) = 3
    c: DistanceX(g-3,g1) = 18
    c: Equal(g0,g2) = 3
    c: DistanceX(g2,g-3) = 0
    c: DistanceY(g1,g-3) = 2.85
    c: DistanceY(g2,g1) = 12.6
    c: DistanceY(g1,g0) = 0
    c: DistanceX(g0,g-3) = 18
FEATURE [Sketcher::SketchObject] Sketch025
  FullyConstrained = false
  MapMode = 5
  Placement = pos=(0,0,0) rot=(1,0,0;1.5708rad)
  Support = -> [XZ_Plane006]
  sketch-geometry (6):
    g0: LineSegment StartX=232.036 StartY=-3.87518 StartZ=0 EndX=252.998 EndY=-3.87518 EndZ=0
    g1: LineSegment StartX=252.998 StartY=-3.87518 StartZ=0 EndX=262.998 EndY=-5.37518 EndZ=0
    g2: LineSegment StartX=262.998 StartY=-5.37518 StartZ=0 EndX=262.998 EndY=-8.37518 EndZ=0
    g3: LineSegment StartX=262.998 StartY=-8.37518 StartZ=0 EndX=252.998 EndY=-9.87518 EndZ=0
    g4: LineSegment StartX=252.998 StartY=-9.87518 StartZ=0 EndX=232.036 EndY=-9.87518 EndZ=0
    g5: LineSegment StartX=232.036 StartY=-9.87518 StartZ=0 EndX=232.036 EndY=-3.87518 EndZ=0
  constraints (15):
    c: Horizontal(g0)
    c: Coincident(g1,g0)
    c: Vertical(g2)
    c: Horizontal(g4)
    c: Coincident(g5,g0)
    c: Vertical(g5)
    c: DistanceY(g5,g5) = 6
    c: Coincident(g1,g2)
    c: Coincident(g2,g3)
    c: Coincident(g3,g4)
    c: Coincident(g4,g5)
    c: DistanceY(g1,g0) = 1.5
    c: DistanceY(g3,g2) = 1.5
    c: DistanceX(g0,g3) = 0
    c: DistanceX(g0,g1) = 10
FEATURE [PartDesign::Pad] Pad013  label="bumper body"
  Direction = (0,-1,-2e-16)
  Length = 10
  Length2 = 10
  Placement = pos=(0,0,0) rot=(1,0,0;1.5708rad)
  Profile = -> Sketch025
  ReferenceAxis = -> Sketch025 [N_Axis]
  Refine = true
  Type = 0
FEATURE [Sketcher::SketchObject] Sketch027
  ExternalGeometry = -> [Sketch025]
  FullyConstrained = false
  MapMode = 5
  Placement = pos=(0,0,0) rot=(-1,0,0;1.5708rad)
  Support = -> [Pad013]
  sketch-geometry (1):
    g0: Circle CenterX=256.37 CenterY=6.87518 CenterZ=0 NormalX=0 NormalY=0 NormalZ=1 AngleXU=0 Radius=1.75
  constraints (2):
    c: Diameter(g0) = 3.5
    c: DistanceY(g0,g-4) = 3
FEATURE [Sketcher::SketchObject] Sketch026
  ExternalGeometry = -> [Sketch025]
  FullyConstrained = true
  MapMode = 5
  Placement = pos=(0,-10,-2.2e-15) rot=(1,0,0;1.5708rad)
  Support = -> [Pad013]
  sketch-geometry (4):
    g0: LineSegment StartX=252.898 StartY=-3.87518 StartZ=0 EndX=252.898 EndY=-8.87518 EndZ=0
    g1: LineSegment StartX=252.898 StartY=-8.87518 StartZ=0 EndX=260.998 EndY=-7.37518 EndZ=0
    g2: LineSegment StartX=260.998 StartY=-7.37518 StartZ=0 EndX=260.998 EndY=-5.87518 EndZ=0
    g3: LineSegment StartX=260.998 StartY=-5.87518 StartZ=0 EndX=252.898 EndY=-3.87518 EndZ=0
  constraints (12):
    c: Vertical(g0)
    c: Vertical(g2)
    c: Coincident(g3,g0)
    c: DistanceX(g0,g-3) = 0.1
    c: DistanceY(g0,g-3) = 0
    c: DistanceY(g-4,g0) = 1
    c: DistanceX(g3,g-6) = 2
    c: Coincident(g1,g0)
    c: Coincident(g3,g2)
    c: Coincident(g1,g2)
    c: DistanceY(g2,g-6) = 0.5
    c: DistanceY(g-5,g1) = 1
FEATURE [PartDesign::Plane] DatumPlane003
  Length = 60
  MapMode = 5
  Placement = pos=(232.036,0,0) rot=(0.707107,0,-0.707107;3.14159rad)
  ResizeMode = 0
  Support = -> [Pad013]
  Width = 60
FEATURE [Sketcher::SketchObject] Sketch036
  ExternalGeometry = -> [Pad013]
  FullyConstrained = false
  MapMode = 5
  Placement = pos=(232.036,0,0) rot=(0.707107,0,-0.707107;3.14159rad)
  Support = -> [DatumPlane003]
  sketch-geometry (18):
    g0: LineSegment StartX=3.87518 StartY=10 StartZ=0 EndX=3.87518 EndY=13.5771 EndZ=0
    g1: LineSegment StartX=7.87518 StartY=13.5771 StartZ=0 EndX=7.87518 EndY=10 EndZ=0
    g2: LineSegment StartX=7.87518 StartY=10 StartZ=0 EndX=6.87518 EndY=10 EndZ=0
    g3: LineSegment StartX=6.87518 StartY=10 StartZ=0 EndX=6.87518 EndY=13 EndZ=0
    g4: LineSegment StartX=4.87518 StartY=13 StartZ=0 EndX=4.87518 EndY=10 EndZ=0
    g5: LineSegment StartX=4.87518 StartY=10 StartZ=0 EndX=3.87518 EndY=10 EndZ=0
    g6: Circle CenterX=4.87518 CenterY=13 CenterZ=0 NormalX=0 NormalY=0 NormalZ=1 AngleXU=0 Radius=1
    g7: Circle CenterX=5.87518 CenterY=14.5514 CenterZ=0 NormalX=0 NormalY=0 NormalZ=1 AngleXU=0 Radius=1
    g8: Circle CenterX=6.87518 CenterY=13 CenterZ=0 NormalX=0 NormalY=0 NormalZ=1 AngleXU=0 Radius=1
    g9: BSplineCurve PolesCount=3 KnotsCount=2 Degree=2 IsPeriodic=0
    g10: GeomPoint X=4.87518 Y=13 Z=0
    g11: GeomPoint X=6.87518 Y=13 Z=0
    g12: Circle CenterX=3.87518 CenterY=13.5771 CenterZ=0 NormalX=0 NormalY=0 NormalZ=1 AngleXU=0 Radius=1
    g13: Circle CenterX=5.87518 CenterY=16.1622 CenterZ=0 NormalX=0 NormalY=0 NormalZ=1 AngleXU=0 Radius=1
    g14: Circle CenterX=7.87518 CenterY=13.5771 CenterZ=0 NormalX=0 NormalY=0 NormalZ=1 AngleXU=0 Radius=1
    g15: BSplineCurve PolesCount=3 KnotsCount=2 Degree=2 IsPeriodic=0
    g16: GeomPoint X=3.87518 Y=13.5771 Z=0
    g17: GeomPoint X=7.87518 Y=13.5771 Z=0
  constraints (38):
    c: Vertical(g0)
    c: Coincident(g1,g2)
    c: Horizontal(g2)
    c: Coincident(g2,g3)
    c: Vertical(g4)
    c: Coincident(g4,g5)
    c: Coincident(g5,g0)
    c: Horizontal(g5)
    c: Vertical(g3)
    c: Vertical(g1)
    c: Distance(g5) = 1
    c: Distance(g2) = 1
    c: Weight(g6) = 1
    c: Coincident(g9,g4)
    c: Equal(g6,g7)
    c: Equal(g6,g8)
    c: Coincident(g9,g3)
    c: InternalAlignment(g6,g9)
    c: InternalAlignment(g7,g9)
    c: InternalAlignment(g8,g9)
    c: InternalAlignment(g10,g9)
    c: InternalAlignment(g11,g9)
    c: Weight(g12) = 1
    c: Coincident(g15,g0)
    c: Equal(g12,g13)
    c: Equal(g12,g14)
    c: Coincident(g15,g1)
    c: InternalAlignment(g12,g15)
    c: InternalAlignment(g13,g15)
    c: InternalAlignment(g14,g15)
    c: InternalAlignment(g16,g15)
    c: InternalAlignment(g17,g15)
    c: DistanceY(g0,g1) = 0
    c: DistanceY(g3,g6) = 0
    c: DistanceX(g4,g2) = 2
    c: DistanceX(g7,g13) = 0
    c: DistanceX(g4,g7) = 1
    c: DistanceX(g-3,g0) = 0
FEATURE [Sketcher::SketchObject] Sketch037
  ExternalGeometry = -> [Pad002]
  FullyConstrained = true
  MapMode = 5
  Placement = pos=(0,12,0) rot=(1,0,0;1.5708rad)
  Support = -> [Pad002]
  expr: Constraints[7] = (<<param>>.mount_body_width - <<param>>.clip_width) / 2 - <<param>>.wall_thickness
  expr: Constraints[8] = <<param>>.mount_body_height
  sketch-geometry (4):
    g0: LineSegment StartX=2 StartY=12 StartZ=0 EndX=2 EndY=0 EndZ=0
    g1: LineSegment StartX=2 StartY=0 StartZ=0 EndX=10.5 EndY=0 EndZ=0
    g2: LineSegment StartX=10.5 StartY=0 StartZ=0 EndX=10.5 EndY=3 EndZ=0
    g3: LineSegment StartX=10.5 StartY=3 StartZ=0 EndX=2 EndY=12 EndZ=0
  constraints (11):
    c: Vertical(g0)
    c: Coincident(g0,g1)
    c: Horizontal(g1)
    c: Coincident(g1,g2)
    c: Vertical(g2)
    c: Coincident(g2,g3)
    c: Coincident(g3,g0)
    c: Distance(g1) = 8.5
    c: Distance(g0) = 12
    c: Distance(g2) = 3
    c: Coincident(g-3,g0)
FEATURE [PartDesign::Pad] Pad017  label="mount slider"
  BaseFeature = -> Pad002
  Direction = (0,-1,2e-16)
  Length = 10
  Length2 = 10
  Profile = -> Sketch037
  ReferenceAxis = -> Sketch037 [N_Axis]
  Refine = true
  Type = 0
  expr: Length = <<param>>.mount_body_depth - 2 * <<param>>.wall_thickness
FEATURE [PartDesign::Pocket] Pocket  label="rail drills"
  BaseFeature = -> Pad017
  Direction = (1,0,0)
  Length = 4
  Length2 = 5
  Profile = -> Sketch004
  ReferenceAxis = -> Sketch004 [N_Axis]
  Refine = true
  Type = 0
  expr: Length = <<param>>.wall_thickness * 2
FEATURE [PartDesign::Pocket] Pocket001  label="tower drill"
  BaseFeature = -> Pocket
  Direction = (1,0,0)
  Length = 2
  Length2 = 5
  Profile = -> Sketch003
  ReferenceAxis = -> Sketch003 [N_Axis]
  Refine = true
  Type = 0
  expr: Length = <<param>>.wall_thickness
FEATURE [PartDesign::Mirrored] Mirrored
  BaseFeature = -> Pocket001
  MirrorPlane = -> DatumPlane
  Originals = -> [Pad001,Pad002,Pocket,Pocket001,Pad017]
  Refine = true
FEATURE [PartDesign::Chamfer] Chamfer004
  Angle = 60
  Base = -> Mirrored [Edge45,Edge43]
  BaseFeature = -> Mirrored
  ChamferType = 2
  FlipDirection = false
  Refine = true
  Size = 1.5
  Size2 = 1
  SupportTransform = false
  UseAllEdges = false
  expr: Size = <<param>>.wall_thickness - 0.5 mm
FEATURE [PartDesign::Body] Body  label="mount"
  Group = -> [Sketch,Pad,Sketch001,Sketch002,Pad001,Pad002,Pad017,Sketch003,DatumPlane,Sketch004,Pocket,Pocket001,Mirrored,Sketch037,Chamfer004]
  Origin = -> Origin
  Tip = -> Chamfer004
FEATURE [Sketcher::SketchObject] Sketch038
  ExternalGeometry = -> [Sketch018]
  FullyConstrained = false
  MapMode = 5
  Placement = pos=(0,0,23.4729) rot=(0,0,1;3.14159rad)
  Support = -> [Pad010]
  sketch-geometry (8):
    g0: LineSegment StartX=-229.786 StartY=1.5 StartZ=0 EndX=-229.786 EndY=5.1e-15 EndZ=0
    g1: LineSegment StartX=-229.786 StartY=5.1e-15 StartZ=0 EndX=-258.549 EndY=5.1e-15 EndZ=0
    g2: Circle CenterX=-258.549 CenterY=5.1e-15 CenterZ=0 NormalX=0 NormalY=0 NormalZ=1 AngleXU=0 Radius=1
    g3: Circle CenterX=-255.981 CenterY=1.23267 CenterZ=0 NormalX=0 NormalY=0 NormalZ=1 AngleXU=0 Radius=1
    g4: Circle CenterX=-229.786 CenterY=1.5 CenterZ=0 NormalX=0 NormalY=0 NormalZ=1 AngleXU=0 Radius=1
    g5: BSplineCurve PolesCount=3 KnotsCount=2 Degree=2 IsPeriodic=0
    g6: GeomPoint X=-258.549 Y=5.2e-15 Z=0
    g7: GeomPoint X=-229.786 Y=1.5 Z=0
  constraints (15):
    c: Coincident(g0,g-3)
    c: Vertical(g0)
    c: Coincident(g0,g1)
    c: Horizontal(g1)
    c: Weight(g2) = 1
    c: Coincident(g5,g1)
    c: Equal(g2,g3)
    c: Equal(g2,g4)
    c: Coincident(g5,g0)
    c: InternalAlignment(g2,g5)
    c: InternalAlignment(g3,g5)
    c: InternalAlignment(g4,g5)
    c: InternalAlignment(g6,g5)
    c: InternalAlignment(g7,g5)
    c: Distance(g0) = 1.5
FEATURE [PartDesign::Plane] DatumPlane004  label="grill center001"
  Length = 60
  MapMode = 5
  Placement = pos=(229.786,0,0) rot=(0.707107,0,-0.707107;3.14159rad)
  ResizeMode = 0
  Support = -> [Pad010]
  Width = 60
FEATURE [Sketcher::SketchObject] Sketch022
  FullyConstrained = false
  MapMode = 5
  Placement = pos=(229.786,0,0) rot=(0.707107,0,-0.707107;3.14159rad)
  Support = -> [DatumPlane004]
  sketch-geometry (5):
    g0: LineSegment StartX=-5.89636 StartY=4 StartZ=0 EndX=-13.3021 EndY=5.29869 EndZ=0
    g1: LineSegment StartX=-13.3021 StartY=5.29869 StartZ=0 EndX=-17.513 EndY=3.98095 EndZ=0
    g2: LineSegment StartX=-5.89636 StartY=0.620886 StartZ=0 EndX=-5.89636 EndY=4 EndZ=0
    g3: LineSegment StartX=-5.89636 StartY=0.620886 StartZ=0 EndX=-17.513 EndY=0.620886 EndZ=0
    g4: LineSegment StartX=-17.513 StartY=0.620886 StartZ=0 EndX=-17.513 EndY=3.98095 EndZ=0
  constraints (5):
    c: Coincident(g1,g0)
    c: Coincident(g2,g0)
    c: Coincident(g3,g2)
    c: Horizontal(g3)
    c: Vertical(g4)
FEATURE [PartDesign::Pad] Pad012  label="grill fins"
  BaseFeature = -> Chamfer001
  Direction = (-1,0,-2e-16)
  Length = 14
  Length2 = 10
  Placement = pos=(0,0,0) rot=(1,0,0;1.5708rad)
  Profile = -> Sketch022
  ReferenceAxis = -> Sketch022 [N_Axis]
  Refine = true
  Reversed = true
  Type = 0
FEATURE [PartDesign::Pocket] Pocket019  label="grill roundout"
  BaseFeature = -> Pad012
  Direction = (0,0,-1)
  Length = 20
  Length2 = 5
  Placement = pos=(0,0,0) rot=(1,0,0;1.5708rad)
  Profile = -> Sketch038
  ReferenceAxis = -> Sketch038 [N_Axis]
  Refine = true
  Type = 0
FEATURE [PartDesign::Mirrored] Mirrored003
  BaseFeature = -> Pocket019
  MirrorPlane = -> DatumPlane004
  Originals = -> [Pad010,Pocket008,Pocket009,Pad011,Chamfer001,Pad012,Pocket019]
  Placement = pos=(0,0,0) rot=(1,0,0;1.5708rad)
  Refine = true
FEATURE [Sketcher::SketchObject] Sketch023
  ExternalGeometry = -> [Mirrored003]
  FullyConstrained = true
  MapMode = 5
  Placement = pos=(0,0,0) rot=(-1,0,0;1.5708rad)
  Support = -> [Pad010]
  sketch-geometry (16):
    g0: LineSegment StartX=215.786 StartY=-16.4533 StartZ=0 EndX=219.786 EndY=-16.4533 EndZ=0
    g1: LineSegment StartX=219.786 StartY=-16.4533 StartZ=0 EndX=219.786 EndY=-5.89636 EndZ=0
    g2: LineSegment StartX=219.786 StartY=-5.89636 StartZ=0 EndX=215.786 EndY=-5.89636 EndZ=0
    g3: LineSegment StartX=215.786 StartY=-5.89636 StartZ=0 EndX=215.786 EndY=-16.4533 EndZ=0
    g4: LineSegment StartX=223.786 StartY=-16.4533 StartZ=0 EndX=227.786 EndY=-16.4533 EndZ=0
    g5: LineSegment StartX=227.786 StartY=-16.4533 StartZ=0 EndX=227.786 EndY=-5.89636 EndZ=0
    g6: LineSegment StartX=227.786 StartY=-5.89636 StartZ=0 EndX=223.786 EndY=-5.89636 EndZ=0
    g7: LineSegment StartX=223.786 StartY=-5.89636 StartZ=0 EndX=223.786 EndY=-16.4533 EndZ=0
    g8: LineSegment StartX=231.786 StartY=-16.4533 StartZ=0 EndX=235.786 EndY=-16.4533 EndZ=0
    g9: LineSegment StartX=235.786 StartY=-16.4533 StartZ=0 EndX=235.786 EndY=-5.89636 EndZ=0
    g10: LineSegment StartX=235.786 StartY=-5.89636 StartZ=0 EndX=231.786 EndY=-5.89636 EndZ=0
    g11: LineSegment StartX=231.786 StartY=-5.89636 StartZ=0 EndX=231.786 EndY=-16.4533 EndZ=0
    g12: LineSegment StartX=239.786 StartY=-16.4533 StartZ=0 EndX=243.786 EndY=-16.4533 EndZ=0
    g13: LineSegment StartX=243.786 StartY=-16.4533 StartZ=0 EndX=243.786 EndY=-5.89636 EndZ=0
    g14: LineSegment StartX=243.786 StartY=-5.89636 StartZ=0 EndX=239.786 EndY=-5.89636 EndZ=0
    g15: LineSegment StartX=239.786 StartY=-5.89636 StartZ=0 EndX=239.786 EndY=-16.4533 EndZ=0
  constraints (46):
    c: Coincident(g0,g1)
    c: Coincident(g1,g2)
    c: Coincident(g2,g3)
    c: Coincident(g3,g0)
    c: Horizontal(g0)
    c: Horizontal(g2)
    c: Vertical(g1)
    c: Vertical(g3)
    c: Coincident(g0,g-4)
    c: Coincident(g4,g5)
    c: Coincident(g5,g6)
    c: Coincident(g6,g7)
    c: Coincident(g7,g4)
    c: Horizontal(g4)
    c: Horizontal(g6)
    c: Vertical(g5)
    c: Vertical(g7)
    c: Coincident(g8,g9)
    c: Coincident(g9,g10)
    c: Coincident(g10,g11)
    c: Coincident(g11,g8)
    c: Horizontal(g8)
    c: Horizontal(g10)
    c: Vertical(g9)
    c: Vertical(g11)
    c: Coincident(g12,g13)
    c: Coincident(g13,g14)
    c: Coincident(g14,g15)
    c: Coincident(g15,g12)
    c: Horizontal(g12)
    c: Horizontal(g14)
    c: Vertical(g13)
    c: Vertical(g15)
    c: Distance(g2) = 4
    c: Distance(g6) = 4
    c: Distance(g10) = 4
    c: Distance(g14) = 4
    c: DistanceY(g2,g-6) = 0
    c: DistanceY(g6,g1) = 0
    c: DistanceY(g13,g-7) = 0
    c: DistanceY(g9,g14) = 0
    c: Coincident(g12,g-5)
    c: DistanceY(g4,g0) = 0
    c: DistanceY(g12,g8) = 0
    c: DistanceX(g1,g6) = 4
    c: DistanceX(g9,g14) = 4
FEATURE [PartDesign::Pocket] Pocket010  label="grill fin gaps"
  BaseFeature = -> Mirrored003
  Direction = (0,-1,-2e-16)
  Length = 7
  Length2 = 5
  Placement = pos=(0,0,0) rot=(1,0,0;1.5708rad)
  Profile = -> Sketch023
  ReferenceAxis = -> Sketch023 [N_Axis]
  Refine = true
  Type = 0
FEATURE [PartDesign::Pocket] Pocket011  label="grill mount"
  BaseFeature = -> Pocket010
  Direction = (0,-1,-2e-16)
  Length = 3.5
  Length2 = 5
  Placement = pos=(0,0,0) rot=(1,0,0;1.5708rad)
  Profile = -> Sketch024
  ReferenceAxis = -> Sketch024 [N_Axis]
  Refine = true
  Type = 0
FEATURE [Sketcher::SketchObject] Sketch040
  ExternalGeometry = -> [Pad013]
  FullyConstrained = true
  MapMode = 5
  Placement = pos=(0,0,0) rot=(-1,0,0;1.5708rad)
  Support = -> [Pad013]
  sketch-geometry (6):
    g0: LineSegment StartX=261.998 StartY=6.37518 StartZ=0 EndX=252.998 EndY=4.87518 EndZ=0
    g1: LineSegment StartX=252.998 StartY=4.87518 StartZ=0 EndX=249.998 EndY=4.87518 EndZ=0
    g2: LineSegment StartX=249.998 StartY=4.87518 StartZ=0 EndX=249.998 EndY=8.87518 EndZ=0
    g3: LineSegment StartX=249.998 StartY=8.87518 StartZ=0 EndX=252.998 EndY=8.87518 EndZ=0
    g4: LineSegment StartX=252.998 StartY=8.87518 StartZ=0 EndX=261.998 EndY=7.37518 EndZ=0
    g5: LineSegment StartX=261.998 StartY=7.37518 StartZ=0 EndX=261.998 EndY=6.37518 EndZ=0
  constraints (18):
    c: Coincident(g0,g1)
    c: Horizontal(g1)
    c: Coincident(g1,g2)
    c: Vertical(g2)
    c: Coincident(g2,g3)
    c: Horizontal(g3)
    c: Coincident(g3,g4)
    c: Coincident(g4,g5)
    c: Coincident(g5,g0)
    c: DistanceX(g0,g-3) = 1
    c: DistanceX(g4,g-6) = 1
    c: DistanceX(g-4,g0) = 0
    c: DistanceX(g-5,g3) = 0
    c: DistanceX(g2,g-5) = 3
    c: DistanceY(g-4,g1) = 1
    c: DistanceY(g2,g-5) = 1
    c: DistanceY(g4,g-6) = 1
    c: DistanceY(g-3,g0) = 1
FEATURE [Part::Part2DObjectPython] Circle  # Draft 2D object (typed FeaturePython)
  Area = 12.5664
  FirstAngle = 0
  LastAngle = 0
  MakeFace = true
  Placement = pos=(248.465,-7.3468,-3.87518) rot=(0,0,1;0rad)
  Radius = 2
FEATURE [Part::Part2DObjectPython] Wire  # Draft 2D object (typed FeaturePython)
  Area = 0
  ChamferSize = 0
  Closed = false
  End = (231.535,-14.701,6.784)
  FilletRadius = 2
  Length = 25.6423
  MakeFace = true
  Placement = pos=(248.46,-7.33759,-3.87518) rot=(0,0,1;0rad)
  Points = (3) [(0,0,0),(-4.70964,-7.36345,10.6592),(-16.9249,-7.36345,10.6592)]
  Start = (248.46,-7.33759,-3.87518)
  Subdivisions = 0
FEATURE [Part::Part2DObjectPython] Line  # Draft 2D object (typed FeaturePython)
  Area = 0
  ChamferSize = 0
  Closed = false
  End = (250.329,-2.11219,-3.87518)
  FilletRadius = 0
  Length = 16.4042
  MakeFace = true
  Placement = pos=(244.229,-13.9527,5.70067) rot=(0,0,1;0rad)
  Points = (2) [(0,0,0),(6.09946,11.8405,-9.57585)]
  Start = (244.229,-13.9527,5.70067)
  Subdivisions = 0
FEATURE [Part::Part2DObjectPython] Circle001  # Draft 2D object (typed FeaturePython)
  Area = 3.14159
  FirstAngle = 0
  LastAngle = 0
  MakeFace = true
  Placement = pos=(250.329,-2.11219,-3.87518) rot=(0,0,1;0rad)
  Radius = 1
FEATURE [Sketcher::SketchObject] Sketch042
  ExternalGeometry = -> [Pad013]
  FullyConstrained = true
  MapMode = 5
  Placement = pos=(0,-10,-2.2e-15) rot=(1,0,0;1.5708rad)
  Support = -> [Pad013]
  sketch-geometry (6):
    g0: LineSegment StartX=232.036 StartY=-3.87518 StartZ=0 EndX=252.998 EndY=-3.87518 EndZ=0
    g1: LineSegment StartX=252.998 StartY=-3.87518 StartZ=0 EndX=262.998 EndY=-5.37518 EndZ=0
    g2: LineSegment StartX=262.998 StartY=-5.37518 StartZ=0 EndX=262.998 EndY=-5.27518 EndZ=0
    g3: LineSegment StartX=262.998 StartY=-5.27518 StartZ=0 EndX=252.998 EndY=-1.87518 EndZ=0
    g4: LineSegment StartX=252.998 StartY=-1.87518 StartZ=0 EndX=232.036 EndY=-1.87518 EndZ=0
    g5: LineSegment StartX=232.036 StartY=-1.87518 StartZ=0 EndX=232.036 EndY=-3.87518 EndZ=0
  constraints (15):
    c: Coincident(g0,g-3)
    c: Coincident(g0,g-4)
    c: Coincident(g0,g1)
    c: Coincident(g1,g-5)
    c: Coincident(g1,g2)
    c: Vertical(g2)
    c: Coincident(g2,g3)
    c: Coincident(g3,g4)
    c: Horizontal(g4)
    c: Coincident(g4,g5)
    c: Coincident(g5,g0)
    c: Vertical(g5)
    c: DistanceY(g0,g4) = 2
    c: DistanceY(g1,g2) = 0.1
    c: DistanceX(g3,g0) = 0
FEATURE [PartDesign::Pad] Pad018  label="bumper lip"
  BaseFeature = -> Pad013
  Direction = (0,-1,-2e-16)
  Length = 3.7
  Length2 = 10
  Placement = pos=(0,0,0) rot=(1,0,0;1.5708rad)
  Profile = -> Sketch042
  ReferenceAxis = -> Sketch042 [N_Axis]
  Refine = true
  Reversed = true
  Type = 0
FEATURE [PartDesign::Pocket] Pocket012
  BaseFeature = -> Pad018
  Direction = (0,1,2e-16)
  Length = 5
  Length2 = 5
  Placement = pos=(0,0,0) rot=(1,0,0;1.5708rad)
  Profile = -> Sketch026
  ReferenceAxis = -> Sketch026 [N_Axis]
  Refine = true
  Type = 0
FEATURE [PartDesign::Pocket] Pocket015  label="led"
  BaseFeature = -> Pocket012
  Direction = (0,-1,-2e-16)
  Length = 5
  Length2 = 5
  Placement = pos=(0,0,0) rot=(1,0,0;1.5708rad)
  Profile = -> Sketch027
  ReferenceAxis = -> Sketch027 [N_Axis]
  Refine = true
  Type = 0
FEATURE [Sketcher::SketchObject] Sketch031
  ExternalGeometry = -> [Sketch025]
  FullyConstrained = true
  MapMode = 5
  Placement = pos=(0,0,0) rot=(-1,0,0;1.5708rad)
  Support = -> [Pocket015]
  expr: Constraints[17] = <<param>>.rail_height
  expr: Constraints[18] = <<param>>.wall_thickness
  expr: Constraints[20] = (6 mm - <<param>>.rail_height) / 2
  expr: Constraints[22] = <<param>>.rail_depth
  sketch-geometry (8):
    g0: LineSegment StartX=244.036 StartY=3.87518 StartZ=0 EndX=246.036 EndY=3.87518 EndZ=0
    g1: LineSegment StartX=246.036 StartY=3.87518 StartZ=0 EndX=246.036 EndY=9.87518 EndZ=0
    g2: LineSegment StartX=246.036 StartY=9.87518 StartZ=0 EndX=244.036 EndY=9.87518 EndZ=0
    g3: LineSegment StartX=244.036 StartY=9.87518 StartZ=0 EndX=244.036 EndY=3.87518 EndZ=0
    g4: LineSegment StartX=248.036 StartY=5.12518 StartZ=0 EndX=246.036 EndY=5.12518 EndZ=0
    g5: LineSegment StartX=246.036 StartY=5.12518 StartZ=0 EndX=246.036 EndY=8.62518 EndZ=0
    g6: LineSegment StartX=246.036 StartY=8.62518 StartZ=0 EndX=248.036 EndY=8.62518 EndZ=0
    g7: LineSegment StartX=248.036 StartY=8.62518 StartZ=0 EndX=248.036 EndY=5.12518 EndZ=0
  constraints (24):
    c: Coincident(g0,g1)
    c: Coincident(g1,g2)
    c: Coincident(g2,g3)
    c: Coincident(g3,g0)
    c: Horizontal(g0)
    c: Horizontal(g2)
    c: Vertical(g1)
    c: Vertical(g3)
    c: Coincident(g4,g5)
    c: Coincident(g5,g6)
    c: Coincident(g6,g7)
    c: Coincident(g7,g4)
    c: Horizontal(g4)
    c: Horizontal(g6)
    c: Vertical(g5)
    c: Vertical(g7)
    c: PointOnObject(g5,g1)
    c: Distance(g7) = 3.5
    c: Distance(g0) = 2
    c: Distance(g3) = 6
    c: DistanceY(g0,g4) = 1.25
    c: DistanceY(g2,g-3) = 0
    c: DistanceX(g0,g4) = 2
    c: DistanceX(g-3,g5) = 14
FEATURE [Sketcher::SketchObject] Sketch034
  ExternalGeometry = -> [Sketch031]
  FullyConstrained = false
  MapMode = 5
  Placement = pos=(0,0,0) rot=(-1,0,0;1.5708rad)
  Support = -> [Pad013]
  sketch-geometry (7):
    g0: Circle CenterX=250.036 CenterY=-2.12482 CenterZ=0 NormalX=0 NormalY=0 NormalZ=1 AngleXU=0 Radius=1.15
    g1: LineSegment StartX=244.036 StartY=3.87518 StartZ=0 EndX=244.036 EndY=9.87518 EndZ=0
    g2: LineSegment StartX=244.036 StartY=9.87518 StartZ=0 EndX=250.036 EndY=9.87518 EndZ=0
    g3: LineSegment StartX=250.036 StartY=9.87518 StartZ=0 EndX=250.036 EndY=3.87518 EndZ=0
    g4: LineSegment StartX=248.203 StartY=-5.12482 StartZ=0 EndX=254.203 EndY=-5.12482 EndZ=0
    g5: LineSegment StartX=244.036 StartY=3.87518 StartZ=0 EndX=248.203 EndY=-5.12482 EndZ=0
    g6: LineSegment StartX=250.036 StartY=3.87518 StartZ=0 EndX=254.203 EndY=-5.12482 EndZ=0
  constraints (19):
    c: DistanceX(g-3,g0) = 6
    c: Diameter(g0) = 2.3
    c: DistanceY(g0,g-3) = 12
    c: Coincident(g1,g2)
    c: Coincident(g2,g3)
    c: Horizontal(g2)
    c: Vertical(g1)
    c: Vertical(g3)
    c: Coincident(g-3,g1)
    c: DistanceY(g4,g1) = 9
    c: Horizontal(g4)
    c: Distance(g4) = 6
    c: Coincident(g5,g4)
    c: Coincident(g1,g5)
    c: Equal(g3,g1)
    c: Coincident(g6,g4)
    c: DistanceY(g-5,g1) = 0
    c: Distance(g2) = 6
    c: Coincident(g6,g3)
FEATURE [Sketcher::SketchObject] Sketch035
  ExternalGeometry = -> [Pad013,Sketch031]
  FullyConstrained = false
  MapMode = 5
  Placement = pos=(0,0,-3.87518) rot=(0,0,1;3.14159rad)
  Support = -> [Pad013]
  sketch-geometry (8):
    g0: LineSegment StartX=-252.998 StartY=10 StartZ=0 EndX=-267.169 EndY=4.78895 EndZ=0
    g1: LineSegment StartX=-267.169 StartY=4.78895 StartZ=0 EndX=-267.169 EndY=10 EndZ=0
    g2: LineSegment StartX=-267.169 StartY=10 StartZ=0 EndX=-252.998 EndY=10 EndZ=0
    g3: LineSegment StartX=-244.036 StartY=1.6802 StartZ=0 EndX=-240.387 EndY=4.22558 EndZ=0
    g4: LineSegment StartX=-240.387 StartY=4.22558 StartZ=0 EndX=-232.036 EndY=4.22558 EndZ=0
    g5: LineSegment StartX=-232.036 StartY=4.22558 StartZ=0 EndX=-232.036 EndY=0 EndZ=0
    g6: LineSegment StartX=-232.036 StartY=0 StartZ=0 EndX=-244.036 EndY=0 EndZ=0
    g7: LineSegment StartX=-244.036 StartY=0 StartZ=0 EndX=-244.036 EndY=1.6802 EndZ=0
  constraints (18):
    c: Coincident(g0,g-3)
    c: Coincident(g0,g1)
    c: Vertical(g1)
    c: Coincident(g1,g2)
    c: Coincident(g2,g0)
    c: Horizontal(g2)
    c: Coincident(g3,g4)
    c: Horizontal(g4)
    c: Coincident(g4,g5)
    c: Vertical(g5)
    c: Coincident(g5,g6)
    c: Horizontal(g6)
    c: Coincident(g6,g7)
    c: Coincident(g7,g3)
    c: DistanceX(g4,g-4) = 0
    c: Vertical(g7)
    c: DistanceY(g-5,g6) = 0
    c: DistanceX(g-6,g6) = 0
FEATURE [PartDesign::Pocket] Pocket021
  BaseFeature = -> Pocket015
  Direction = (0,-1,-2e-16)
  Length = 2
  Length2 = 5
  Placement = pos=(0,0,0) rot=(1,0,0;1.5708rad)
  Profile = -> Sketch040
  ReferenceAxis = -> Sketch040 [N_Axis]
  Refine = true
  Type = 0
FEATURE [Sketcher::SketchObject] Sketch041
  ExternalGeometry = -> [Pocket021,Sketch027]
  FullyConstrained = true
  MapMode = 5
  Placement = pos=(0,-2,-2e-16) rot=(-1,0,0;1.5708rad)
  Support = -> [Pocket021]
  sketch-geometry (1):
    g0: Circle CenterX=256.37 CenterY=6.87518 CenterZ=0 NormalX=0 NormalY=0 NormalZ=1 AngleXU=0 Radius=2.25
  constraints (2):
    c: Diameter(g0) = 4.5
    c: Coincident(g0,g-5)
FEATURE [PartDesign::Pocket] Pocket022  label="led drill"
  BaseFeature = -> Pocket021
  Direction = (0,-1,-2e-16)
  Length = 1.5
  Length2 = 5
  Placement = pos=(0,0,0) rot=(1,0,0;1.5708rad)
  Profile = -> Sketch041
  ReferenceAxis = -> Sketch041 [N_Axis]
  Refine = true
  Type = 0
FEATURE [PartDesign::Pad] Pad014  label="bumper rails"
  BaseFeature = -> Pocket022
  Direction = (0,1,2e-16)
  Length = 16
  Length2 = 10
  Placement = pos=(0,0,0) rot=(1,0,0;1.5708rad)
  Profile = -> Sketch031
  ReferenceAxis = -> Sketch031 [N_Axis]
  Refine = true
  Type = 4
FEATURE [PartDesign::Pad] Pad015  label="bumper mount"
  BaseFeature = -> Pad014
  Direction = (0,1,2e-16)
  Length = 7
  Length2 = 10
  Placement = pos=(0,0,0) rot=(1,0,0;1.5708rad)
  Profile = -> Sketch034
  ReferenceAxis = -> Sketch034 [N_Axis]
  Refine = true
  Type = 0
FEATURE [Sketcher::SketchObject] Sketch039
  ExternalGeometry = -> [Sketch031,Pad015,Sketch034]
  FullyConstrained = true
  MapMode = 5
  Placement = pos=(0,0,0) rot=(1,0,0;1.5708rad)
  Support = -> [Pad015]
  sketch-geometry (4):
    g0: LineSegment StartX=254.203 StartY=-3.87518 StartZ=0 EndX=244.036 EndY=-3.87518 EndZ=0
    g1: LineSegment StartX=244.036 StartY=-3.87518 StartZ=0 EndX=244.036 EndY=5.12482 EndZ=0
    g2: LineSegment StartX=244.036 StartY=5.12482 StartZ=0 EndX=254.203 EndY=5.12482 EndZ=0
    g3: LineSegment StartX=254.203 StartY=5.12482 StartZ=0 EndX=254.203 EndY=-3.87518 EndZ=0
  constraints (10):
    c: Coincident(g0,g1)
    c: Coincident(g1,g2)
    c: Coincident(g2,g3)
    c: Horizontal(g0)
    c: Horizontal(g2)
    c: Vertical(g1)
    c: Vertical(g3)
    c: Coincident(g0,g-3)
    c: Coincident(g0,g3)
    c: Coincident(g2,g-7)
FEATURE [PartDesign::Pocket] Pocket020  label="bumper mount cut"
  BaseFeature = -> Pad015
  Direction = (0,1,2e-16)
  Length = 4
  Length2 = 5
  Placement = pos=(0,0,0) rot=(1,0,0;1.5708rad)
  Profile = -> Sketch039
  ReferenceAxis = -> Sketch039 [N_Axis]
  Refine = true
  Type = 0
FEATURE [PartDesign::Pocket] Pocket017
  BaseFeature = -> Pocket020
  Direction = (0,0,-1)
  Length = 20
  Length2 = 5
  Placement = pos=(0,0,0) rot=(1,0,0;1.5708rad)
  Profile = -> Sketch035
  ReferenceAxis = -> Sketch035 [N_Axis]
  Refine = true
  Type = 4
FEATURE [PartDesign::AdditivePipe] AdditivePipe
  AuxilleryCurvelinear = true
  AuxillerySpineTangent = false
  BaseFeature = -> Pocket017
  Binormal = (0,0,0)
  Mode = 0
  Placement = pos=(0,0,0) rot=(1,0,0;1.5708rad)
  Profile = -> Circle
  Refine = true
  Spine = -> Wire
  SpineTangent = false
  Transformation = 0
  Transition = 0
FEATURE [PartDesign::AdditivePipe] AdditivePipe001
  AuxilleryCurvelinear = true
  AuxillerySpineTangent = false
  BaseFeature = -> AdditivePipe
  Binormal = (0,0,0)
  Mode = 0
  Placement = pos=(0,0,0) rot=(1,0,0;1.5708rad)
  Profile = -> Circle001
  Refine = true
  Spine = -> Line
  SpineTangent = false
  Transformation = 0
  Transition = 0
FEATURE [PartDesign::Mirrored] Mirrored004
  BaseFeature = -> AdditivePipe001
  MirrorPlane = -> DatumPlane003
  Originals = -> [Pad013,Pad015,Pad014,Pocket015,Pocket012,Pocket020,Pocket021,Pocket022,AdditivePipe,AdditivePipe001,Pad018,Pocket017]
  Placement = pos=(0,0,0) rot=(1,0,0;1.5708rad)
  Refine = true
FEATURE [PartDesign::Pad] Pad016
  BaseFeature = -> Mirrored004
  Direction = (-1,0,-2e-16)
  Length = 13
  Length2 = 13
  Placement = pos=(0,0,0) rot=(1,0,0;1.5708rad)
  Profile = -> Sketch036
  ReferenceAxis = -> Sketch036 [N_Axis]
  Refine = true
  Type = 4
FEATURE [PartDesign::Pocket] Pocket018  label="tow"
  BaseFeature = -> Pad016
  Direction = (1,0,2e-16)
  Length = 11
  Length2 = 11
  Placement = pos=(0,0,0) rot=(1,0,0;1.5708rad)
  Profile = -> Sketch036
  ReferenceAxis = -> Sketch036 [N_Axis]
  Refine = true
  Type = 4
FEATURE [PartDesign::Chamfer] Chamfer007
  Angle = 45
  Base = -> Pocket018 [Edge42,Edge45,Edge48]
  BaseFeature = -> Pocket018
  ChamferType = 2
  FlipDirection = false
  Placement = pos=(0,0,0) rot=(1,0,0;1.5708rad)
  Refine = true
  Size = 1
  Size2 = 1
  SupportTransform = false
  UseAllEdges = false
FEATURE [PartDesign::Chamfer] Chamfer008
  Angle = 45
  Base = -> Chamfer007 [Edge47]
  BaseFeature = -> Chamfer007
  ChamferType = 0
  FlipDirection = false
  Placement = pos=(0,0,0) rot=(1,0,0;1.5708rad)
  Refine = true
  Size = 0.9
  Size2 = 1
  SupportTransform = false
  UseAllEdges = false
FEATURE [PartDesign::Body] Body006  label="bumper"
  Group = -> [Sketch025,Sketch026,Sketch027,Pad013,Pad018,Pocket012,Pocket015,Pocket021,Pocket022,Sketch031,Pad014,Sketch034,Pad015,Pocket020,DatumPlane003,Sketch035,Pocket017,AdditivePipe,AdditivePipe001,Mirrored004,Pad016,Pocket018,Sketch036,Sketch039,Sketch040,Sketch041,Circle,Wire,Line,Circle001,Sketch042,Chamfer007,Chamfer008]
  Origin = -> Origin006
  Placement = pos=(-79,0,23) rot=(0,0,1;0rad)
  Tip = -> Chamfer008
FEATURE [PartDesign::Chamfer] Chamfer006
  Angle = 45
  Base = -> Pocket011 [Edge106,Edge105,Edge123,Edge122,Edge120,Edge119,Edge142,Edge170,Edge171,Edge145,Edge166,Edge147]
  BaseFeature = -> Pocket011
  ChamferType = 0
  FlipDirection = false
  Placement = pos=(0,0,0) rot=(1,0,0;1.5708rad)
  Refine = true
  Size = 1
  Size2 = 1
  SupportTransform = false
  UseAllEdges = false
FEATURE [PartDesign::Body] Body005  label="grill"
  Group = -> [Sketch018,Pad010,DatumPlane004,Sketch019,Sketch020,Sketch021,Pocket008,Pocket009,Pad011,Chamfer001,Sketch022,Pad012,Pocket019,Mirrored003,Sketch023,Pocket010,Sketch024,Pocket011,Sketch038,Chamfer006]
  Origin = -> Origin005
  Tip = -> Chamfer006
